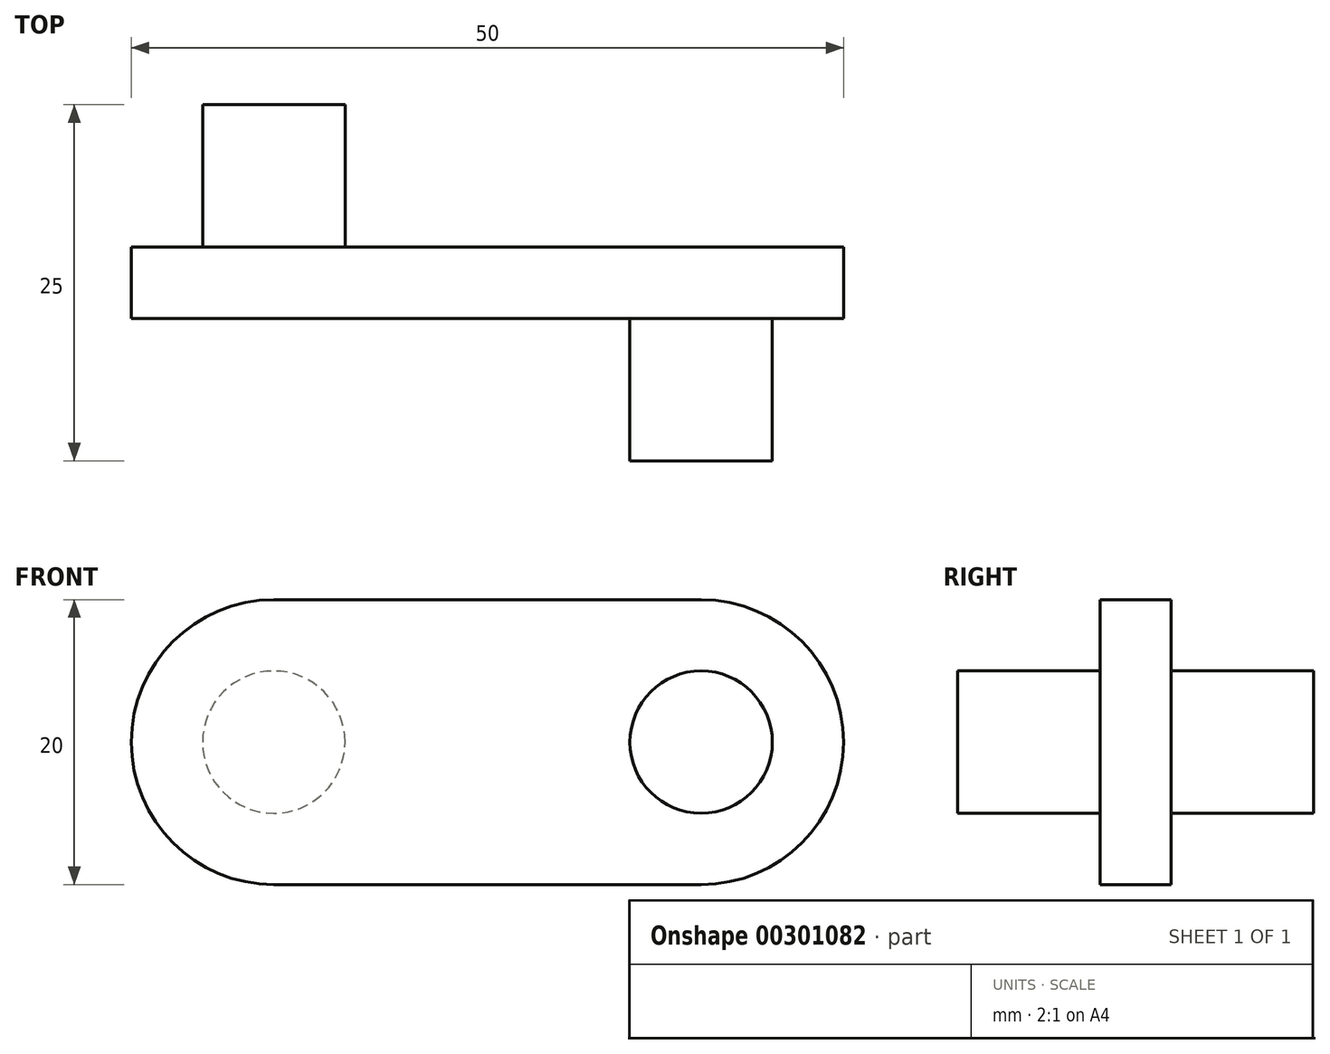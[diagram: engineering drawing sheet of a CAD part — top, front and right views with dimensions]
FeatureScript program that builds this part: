
annotation { "Feature Type Name" : "Feature", "Feature Type Description" : "" }
export const myFeature = defineFeature(function(context is Context, id is Id, definition is map)
    precondition{}
    {
        {
            var Q0;
            Q0=qCreatedBy(makeId("Front.planeOp"),FACE);
            var sketch = newSketch(context, id + "F0", { "sketchPlane" : qUnion([Q0])});
            skCircle(sketch, "E0", {"center": v(0, 0) * mm, "radius": 5 * mm});
            skCircle(sketch, "E1", {"center": v(30, 0) * mm, "radius": 5 * mm});
            skLineSegment(sketch, "E2", {"start": v(0, 10) * mm, "end": v(30, 10) * mm});
            skLineSegment(sketch, "E3", {"start": v(0, -10) * mm, "end": v(30, -10) * mm});
            skArc(sketch, "E4", {"start": v(30, -10) * mm, "mid": v(40, 0) * mm, "end": v(30, 10) * mm});
            skArc(sketch, "E5", {"start": v(0, 10) * mm, "mid": v(-10, 0) * mm, "end": v(0, -10) * mm});
            skSolve(sketch);
        }
        {
            var Q0;
            Q0=makeQuery(id+"F0.imprint","IMPRINT",FACE,{"disambiguationData":[TD([[makeQuery(id+"F0.imprint","IMPRINT",EDGE,{"derivedFrom":sQuery(id+"F0.wireOp",EDGE,"E0")}),1.0]])]});
            extrude(context, id + "F1", {"entities" : qUnion([Q0]), "oppositeDirection" : true, "depth" : 15 * mm});
        }
        {
            var Q0;
            Q0=makeQuery(id+"F0.imprint","IMPRINT",FACE,{"disambiguationData":[TD([[makeQuery(id+"F0.imprint","IMPRINT",EDGE,{"derivedFrom":sQuery(id+"F0.wireOp",EDGE,"E0")}),-1.0]])]});
            extrude(context, id + "F2", {"entities" : qUnion([Q0]), "operationType" : NewBodyOperationType.ADD, "oppositeDirection" : true, "depth" : 5 * mm});
        }
        {
            var Q0;
            Q0=makeQuery(id+"F0.imprint","IMPRINT",FACE,{"disambiguationData":[TD([[makeQuery(id+"F0.imprint","IMPRINT",EDGE,{"derivedFrom":sQuery(id+"F0.wireOp",EDGE,"E1")}),1.0]])]});
            extrude(context, id + "F3", {"entities" : qUnion([Q0]), "operationType" : NewBodyOperationType.ADD, "depth" : 10 * mm, "hasSecondDirection" : true, "secondDirectionOppositeDirection" : true, "secondDirectionDepth" : 5 * mm});
        }
    });
